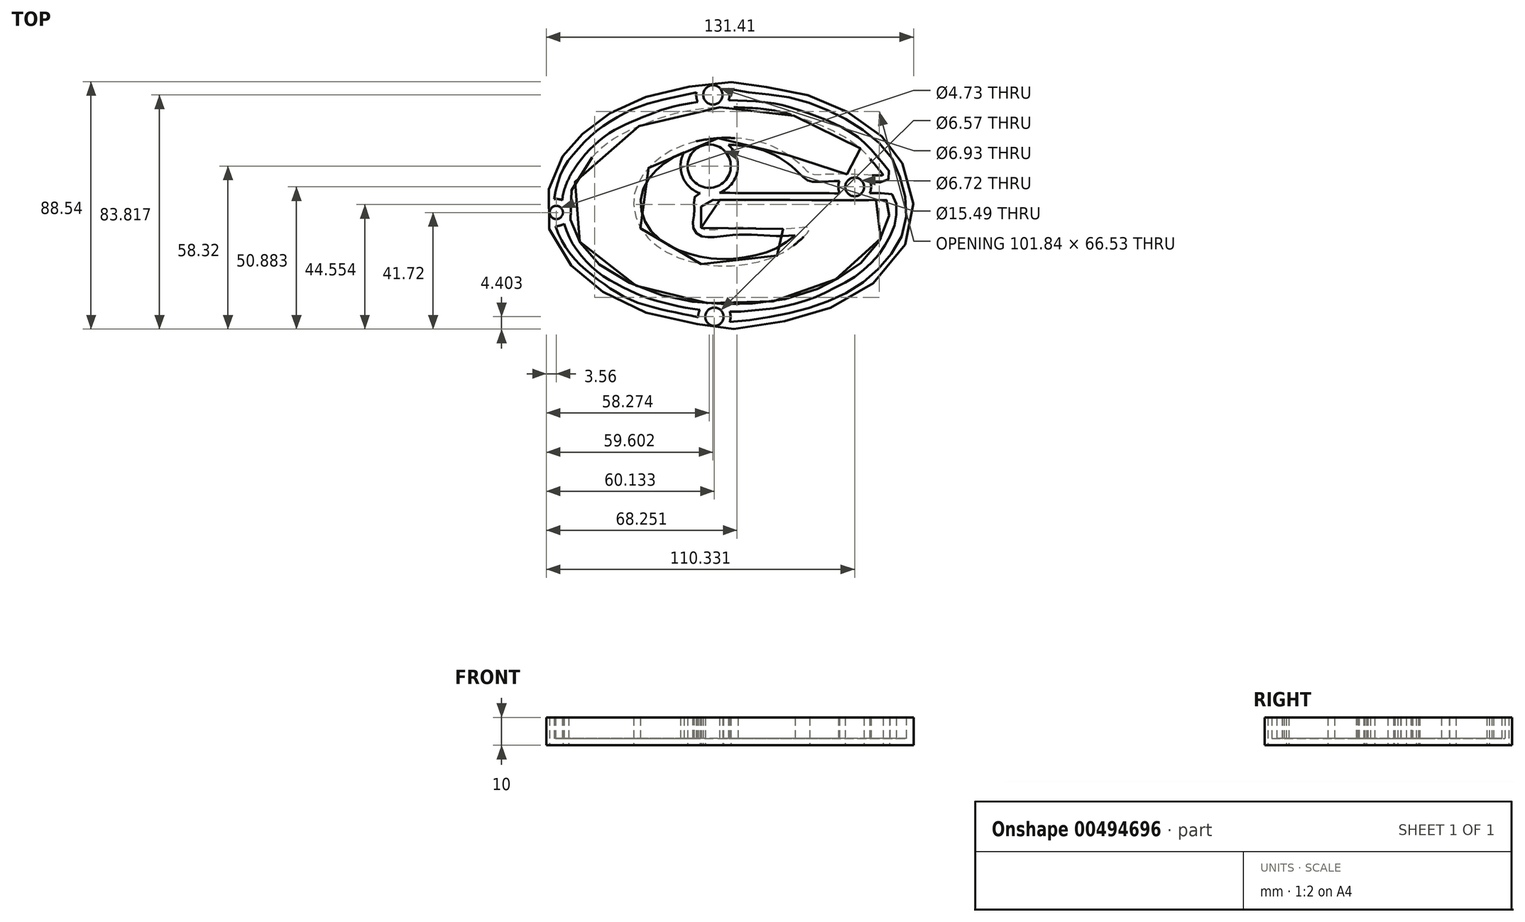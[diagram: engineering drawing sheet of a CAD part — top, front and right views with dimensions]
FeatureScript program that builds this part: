
annotation { "Feature Type Name" : "Feature", "Feature Type Description" : "" }
export const myFeature = defineFeature(function(context is Context, id is Id, definition is map)
    precondition{}
    {
        {
            var Q0;
            Q0=qCreatedBy(makeId("Top.planeOp"),FACE);
            var sketch = newSketch(context, id + "F0", { "sketchPlane" : qUnion([Q0])});
            skFitSpline(sketch, "E0", {"points": [v(-7.95, -5.56) * mm, v(-7.92, -1.3) * mm, v(-7.92, 1.58) * mm, v(-7.97, 4.41) * mm, v(-7.87, 4.46) * mm, v(-4.99, 4.51) * mm, v(2.6, 4.51) * mm, v(10.86, 4.41) * mm, v(17.14, 4.46) * mm, v(27.26, 4.46) * mm, v(40.78, 4.36) * mm, v(51, 4.36) * mm, v(59.07, 4.37) * mm, v(59.35, 4.08) * mm, v(59.42, 2.24) * mm, v(59.07, -3.02) * mm, v(56.8, -8.57) * mm, v(53.24, -13.97) * mm, v(48.34, -18.8) * mm, v(43, -22.64) * mm, v(39.38, -24.34) * mm, v(36.3, -26.07) * mm, v(28.67, -29.15) * mm, v(19.72, -31.48) * mm, v(11.24, -32.5) * mm, v(5.1, -33.06) * mm, v(0, -32.78) * mm, v(-9.82, -32.13) * mm, v(-17.09, -30.73) * mm, v(-25.75, -28.5) * mm, v(-34.8, -24.5) * mm, v(-43.46, -19.27) * mm, v(-49.05, -13.68) * mm, v(-52.12, -9.2) * mm, v(-54.14, -4.48) * mm, v(-55.2, 0) * mm, v(-54.29, 8.13) * mm, v(-48.07, 18.45) * mm, v(-39.1, 26.5) * mm, v(-28.33, 31.66) * mm, v(-15.58, 35.9) * mm, v(-3.58, 37.58) * mm, v(0, 37.73) * mm, v(6.13, 37.58) * mm, v(18.12, 36.51) * mm, v(28.3, 33.63) * mm, v(37.1, 30.29) * mm, v(45.3, 25.89) * mm, v(50.92, 21.03) * mm, v(56.69, 14.2) * mm, v(57.14, 13.44) * mm, v(48.49, 13.6) * mm, v(36.2, 13.6) * mm, v(31.33, 13.74) * mm, v(28.9, 15.87) * mm, v(22.53, 21.03) * mm, v(14.18, 24.98) * mm, v(5.83, 26.5) * mm, v(-3.43, 26.5) * mm, v(-14.36, 24.07) * mm, v(-21.8, 20.27) * mm, v(-28.18, 14.35) * mm, v(-31.06, 9.04) * mm, v(-32.13, 3.27) * mm, v(-30.15, -4.63) * mm, v(-25.3, -10.7) * mm, v(-18.77, -14.95) * mm, v(-9.96, -17.99) * mm, v(0, -19.2) * mm, v(9.47, -18.3) * mm, v(18.73, -15.7) * mm, v(26.47, -10.7) * mm, v(30.88, -5.69) * mm, v(24.8, -5.69) * mm, v(13.87, -5.69) * mm, v(3.1, -5.54) * mm, v(-7.95, -5.56) * mm]});
            skPoint(sketch, "E1.19.internal.snap0", {"position": v(2.63, -41.7) * mm});
            skFitSpline(sketch, "E1", {"points": [v(64.05, 17.6) * mm, v(59.42, 24.73) * mm, v(48.73, 33.36) * mm, v(36.53, 39.76) * mm, v(21.35, 44.22) * mm, v(9.9, 45.41) * mm, v(0, 46.82) * mm, v(-15.84, 44.22) * mm, v(-30.27, 40.5) * mm, v(-41.13, 35.15) * mm, v(-48.87, 29.5) * mm, v(-54.14, 24.07) * mm, v(-58.6, 18.45) * mm, v(-62.5, 8.13) * mm, v(-62.69, -4.48) * mm, v(-55.87, -17.37) * mm, v(-45.93, -26.33) * mm, v(-31.71, -34.5) * mm, v(-9.82, -39.84) * mm, v(0, -41.7) * mm, v(19.24, -39.47) * mm, v(37.56, -34.42) * mm, v(54.2, -24.89) * mm, v(66.16, -9.2) * mm, v(67.84, 4.08) * mm, v(64.05, 17.6) * mm]});
            skCircle(sketch, "E2", {"center": v(-5.05, 16.6) * mm, "radius": 7.74 * mm});
            skCircle(sketch, "E3", {"center": v(47.01, 9.16) * mm, "radius": 3.36 * mm});
            skCircle(sketch, "E4", {"center": v(-3.72, 42.1) * mm, "radius": 3.46 * mm});
            skCircle(sketch, "E5", {"center": v(-3.19, -37.32) * mm, "radius": 3.29 * mm});
            skCircle(sketch, "E6", {"center": v(-59.76, 0) * mm, "radius": 2.36 * mm});
            skSolve(sketch);
        }
        {
            var Q0;
            Q0 = qSketchRegion(id + "F0", true);
            extrude(context, id + "F1", {"entities" : qUnion([Q0]), "depth" : 10 * mm});
        }
        {
            var Q0;
            Q0=makeQuery(id+"F1.opExtrude","CAP_FACE",FACE,{"disambiguationData":[OSD([sQuery(id+"F0.wireOp",EDGE,"E0"),sQuery(id+"F0.wireOp",EDGE,"E1"),sQuery(id+"F0.wireOp",EDGE,"E2"),sQuery(id+"F0.wireOp",EDGE,"E3"),sQuery(id+"F0.wireOp",EDGE,"E4"),sQuery(id+"F0.wireOp",EDGE,"E5"),sQuery(id+"F0.wireOp",EDGE,"E6")])],"isStart":false});
            shell(context, id + "F2", {"entities" : qUnion([Q0]), "thickness" : 2.5 * mm});
        }
    });
